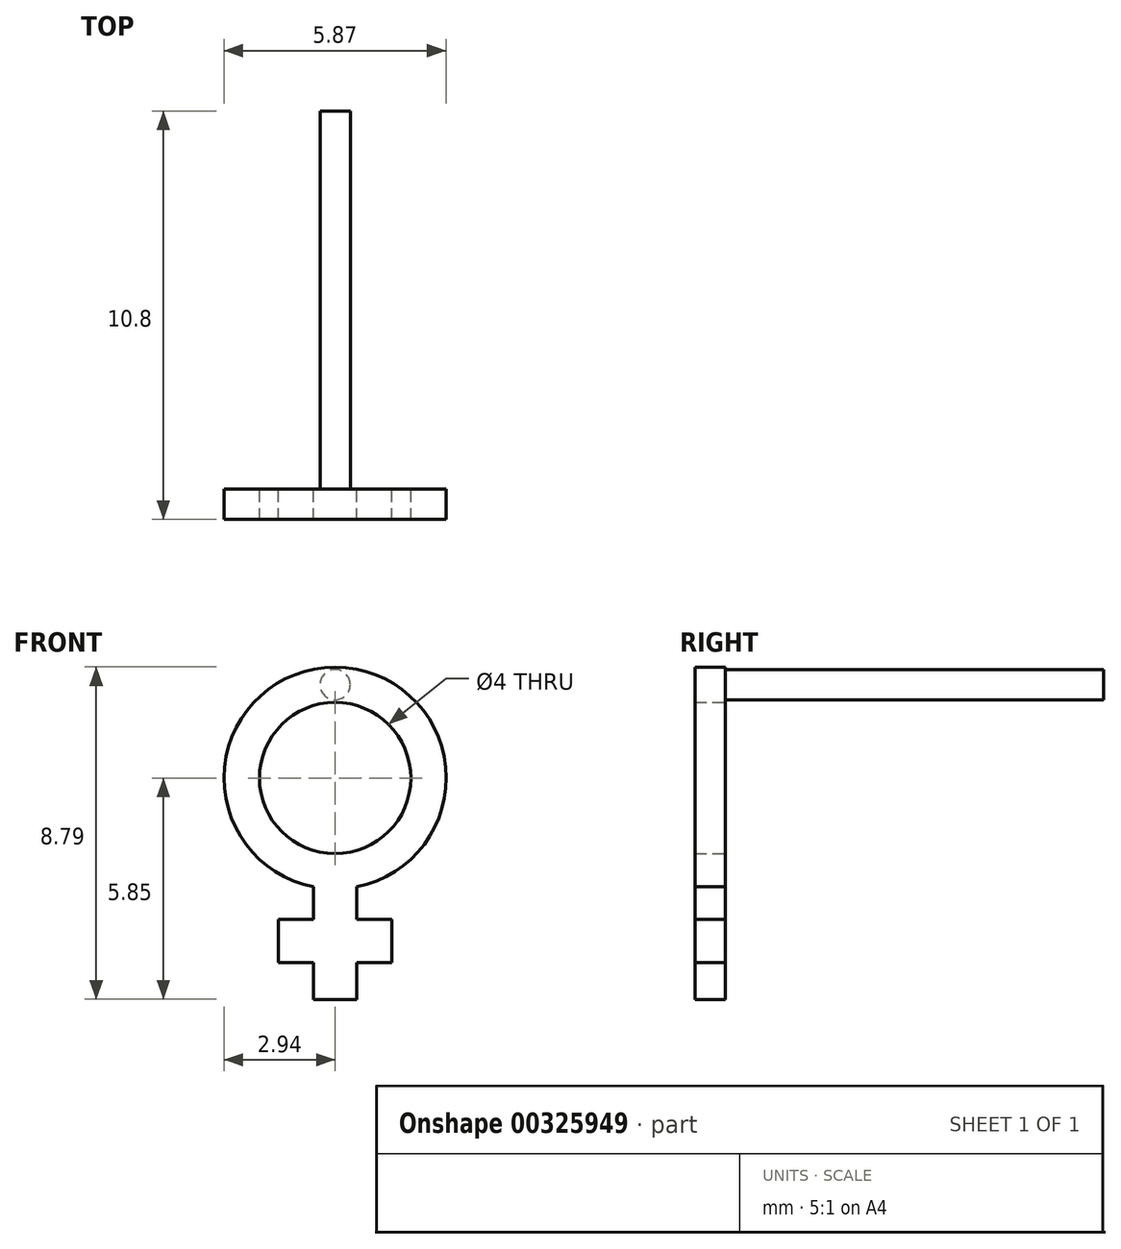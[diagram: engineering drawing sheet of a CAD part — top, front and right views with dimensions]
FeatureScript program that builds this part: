
annotation { "Feature Type Name" : "Feature", "Feature Type Description" : "" }
export const myFeature = defineFeature(function(context is Context, id is Id, definition is map)
    precondition{}
    {
        {
            var Q0;
            Q0=qCreatedBy(makeId("Front.planeOp"),FACE);
            var sketch = newSketch(context, id + "F0", { "sketchPlane" : qUnion([Q0])});
            skCircle(sketch, "E0", {"center": v(0, 0) * mm, "radius": 2.94 * mm});
            skCircle(sketch, "E1", {"center": v(0, 0) * mm, "radius": 2 * mm});
            skLineSegment(sketch, "E2", {"start": v(0, -2.94) * mm, "end": v(0, -5.85) * mm});
            skLineSegment(sketch, "E3", {"start": v(0, -5.85) * mm, "end": v(0.57, -5.85) * mm});
            skLineSegment(sketch, "E4", {"start": v(0.57, -2.88) * mm, "end": v(0.57, -3.74) * mm});
            skLineSegment(sketch, "E5", {"start": v(1.5, -3.74) * mm, "end": v(0, -3.74) * mm});
            skLineSegment(sketch, "E6", {"start": v(1.5, -3.74) * mm, "end": v(1.5, -4.88) * mm});
            skLineSegment(sketch, "E7", {"start": v(1.5, -4.88) * mm, "end": v(0.57, -4.88) * mm});
            skLineSegment(sketch, "E8", {"start": v(0.57, -4.88) * mm, "end": v(0.57, -5.85) * mm});
            skLineSegment(sketch, "E9.MirrorCS", {"start": v(-0.57, -2.88) * mm, "end": v(-0.57, -3.74) * mm});
            skLineSegment(sketch, "E10.MirrorCS", {"start": v(-1.5, -3.74) * mm, "end": v(0, -3.74) * mm});
            skLineSegment(sketch, "E11.MirrorCS", {"start": v(-1.5, -3.74) * mm, "end": v(-1.5, -4.88) * mm});
            skLineSegment(sketch, "E12.MirrorCS", {"start": v(-1.5, -4.88) * mm, "end": v(-0.57, -4.88) * mm});
            skLineSegment(sketch, "E13.MirrorCS", {"start": v(-0.57, -4.88) * mm, "end": v(-0.57, -5.85) * mm});
            skLineSegment(sketch, "E14.MirrorCS", {"start": v(0, -5.85) * mm, "end": v(-0.57, -5.85) * mm});
            skSolve(sketch);
        }
        {
            var Q0;
            Q0=makeQuery(id+"F0.imprint","IMPRINT",FACE,{"disambiguationData":[TD([[makeQuery(id+"F0.imprint","IMPRINT",EDGE,{"derivedFrom":sQuery(id+"F0.wireOp",EDGE,"E1")}),-1.0]])]});
            var Q1;
            {var subQ3=sQuery(id+"F0.wireOp",EDGE,"E3");Q1=makeQuery(id+"F0.imprint","IMPRINT",FACE,{"disambiguationData":[TD([[makeQuery(id+"F0.imprint","IMPRINT",EDGE,{"derivedFrom":subQ3}),1.0]])]});}
            var Q2;
            {var subQ0=sQuery(id+"F0.wireOp",EDGE,"E4");Q2=makeQuery(id+"F0.imprint","IMPRINT",FACE,{"disambiguationData":[TD([[makeQuery(id+"F0.imprint","IMPRINT",EDGE,{"derivedFrom":subQ0}),-1.0]])]});}
            var Q3;
            {var subQ0=sQuery(id+"F0.wireOp",EDGE,"E9.MirrorCS");Q3=makeQuery(id+"F0.imprint","IMPRINT",FACE,{"disambiguationData":[TD([[makeQuery(id+"F0.imprint","IMPRINT",EDGE,{"derivedFrom":subQ0}),1.0]])]});}
            var Q4;
            {var subQ0=sQuery(id+"F0.wireOp",EDGE,"E11.MirrorCS");Q4=makeQuery(id+"F0.imprint","IMPRINT",FACE,{"disambiguationData":[TD([[makeQuery(id+"F0.imprint","IMPRINT",EDGE,{"derivedFrom":subQ0}),1.0]])]});}
            extrude(context, id + "F1", {"entities" : qUnion([Q0, Q1, Q2, Q3, Q4]), "depth" : .8 * mm, "offsetDistance" : 25.4 * mm});
        }
        {
            var Q0;
            Q0=makeQuery(id+"F1.opExtrude","CAP_FACE",FACE,{"disambiguationData":[OSD([sQuery(id+"F0.wireOp",EDGE,"E0"),sQuery(id+"F0.wireOp",EDGE,"E1"),sQuery(id+"F0.wireOp",EDGE,"E3"),sQuery(id+"F0.wireOp",EDGE,"E4"),sQuery(id+"F0.wireOp",EDGE,"E5"),sQuery(id+"F0.wireOp",EDGE,"E6"),sQuery(id+"F0.wireOp",EDGE,"E7"),sQuery(id+"F0.wireOp",EDGE,"E8"),sQuery(id+"F0.wireOp",EDGE,"E9.MirrorCS"),sQuery(id+"F0.wireOp",EDGE,"E10.MirrorCS"),sQuery(id+"F0.wireOp",EDGE,"E11.MirrorCS"),sQuery(id+"F0.wireOp",EDGE,"E12.MirrorCS"),sQuery(id+"F0.wireOp",EDGE,"E13.MirrorCS"),sQuery(id+"F0.wireOp",EDGE,"E14.MirrorCS")])],"isStart":true});
            var sketch = newSketch(context, id + "F2", { "sketchPlane" : qUnion([Q0])});
            skCircle(sketch, "E15", {"center": v(0, 2.47) * mm, "radius": 0.4 * mm});
            skPoint(sketch, "E16", {"position": v(0, 2.93) * mm});
            skSolve(sketch);
        }
        {
            var Q0;
            Q0=makeQuery(id+"F2.imprint","IMPRINT",FACE,{"disambiguationData":[TD([[makeQuery(id+"F2.imprint","IMPRINT",EDGE,{"derivedFrom":sQuery(id+"F2.wireOp",EDGE,"E15")}),1.0]])]});
            extrude(context, id + "F3", {"entities" : qUnion([Q0]), "operationType" : NewBodyOperationType.ADD, "depth" : 10 * mm, "offsetDistance" : 25.4 * mm});
        }
    });
